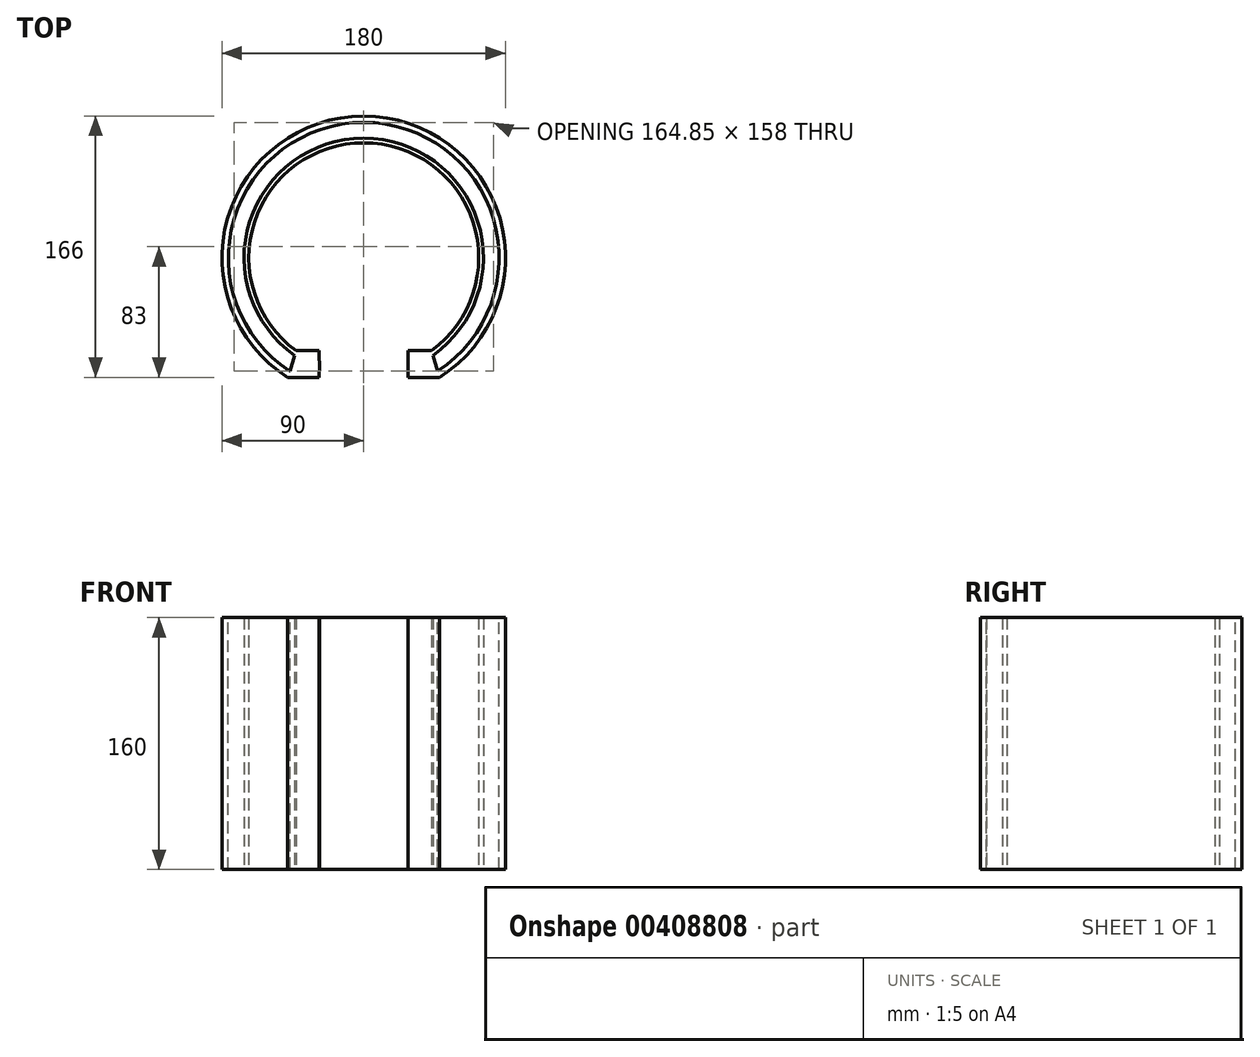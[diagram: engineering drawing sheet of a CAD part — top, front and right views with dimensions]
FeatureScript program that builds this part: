
annotation { "Feature Type Name" : "Feature", "Feature Type Description" : "" }
export const myFeature = defineFeature(function(context is Context, id is Id, definition is map)
    precondition{}
    {
        {
            var Q0;
            Q0=qCreatedBy(makeId("Top.planeOp"),FACE);
            var sketch = newSketch(context, id + "F0", { "sketchPlane" : qUnion([Q0])});
            skArc(sketch, "E0", {"start": v(48.2, -76) * mm, "mid": v(0, 90) * mm, "end": v(-48.2, -76) * mm});
            skLineSegment(sketch, "E1", {"start": v(-48.2, -76) * mm, "end": v(48.2, -76) * mm});
            skCircle(sketch, "E2", {"center": v(0, 0) * mm, "radius": 45 * mm, "construction": true});
            skSolve(sketch);
        }
        {
            var Q0;
            Q0=makeQuery(id+"F0.imprint","IMPRINT",FACE,{"disambiguationData":[TD([[makeQuery(id+"F0.imprint","IMPRINT",EDGE,{"derivedFrom":sQuery(id+"F0.wireOp",EDGE,"E0")}),1.0]])]});
            extrude(context, id + "F1", {"entities" : qUnion([Q0]), "depth" : 160 * mm});
        }
        {
            var Q0;
            Q0=makeQuery(id+"F1.opExtrude","CAP_FACE",FACE,{"disambiguationData":[OSD([sQuery(id+"F0.wireOp",EDGE,"E0"),sQuery(id+"F0.wireOp",EDGE,"E1")])],"isStart":false});
            var sketch = newSketch(context, id + "F2", { "sketchPlane" : qUnion([Q0])});
            skArc(sketch, "E3.0", {"start": v(47.03, -72) * mm, "mid": v(0, 86) * mm, "end": v(-47.03, -72) * mm});
            skLineSegment(sketch, "E3.1", {"start": v(-47.03, -72) * mm, "end": v(47.03, -72) * mm});
            skSolve(sketch);
        }
        {
            var Q0;
            Q0=makeQuery(id+"F2.imprint","IMPRINT",FACE,{"disambiguationData":[TD([[makeQuery(id+"F2.imprint","IMPRINT",EDGE,{"derivedFrom":sQuery(id+"F2.wireOp",EDGE,"E3.0")}),1.0]])]});
            extrude(context, id + "F3", {"entities" : qUnion([Q0]), "operationType" : NewBodyOperationType.REMOVE, "endBound" : BoundingType.UP_TO_NEXT, "oppositeDirection" : true, "depth" : 154 * mm});
        }
        {
            var Q0;
            Q0=makeQuery(id+"F1.opExtrude","SWEPT_FACE",FACE,{"disambiguationData":[OSD([sQuery(id+"F0.wireOp",EDGE,"E1")])]});
            var sketch = newSketch(context, id + "F4", { "sketchPlane" : qUnion([Q0])});
            skLineSegment(sketch, "E4.0", {"start": v(-28.2, 160) * mm, "end": v(-28.2, 0) * mm});
            skLineSegment(sketch, "E5.0", {"start": v(28.2, 160) * mm, "end": v(28.2, 0) * mm});
            skSolve(sketch);
        }
        {
            var Q0;
            Q0=qSketchRegion(id+"F4",true);
            var Q1;
            {var subQ0=sQuery(id+"F4.wireOp",EDGE,"E4.0");Q1=makeQuery(id+"F4.imprint","IMPRINT",FACE,{"disambiguationData":[TD([[makeQuery(id+"F4.imprint","IMPRINT",EDGE,{"derivedFrom":subQ0}),1.0]])]});}
            extrude(context, id + "F5", {"entities" : qUnion([Q0, Q1]), "operationType" : NewBodyOperationType.REMOVE, "endBound" : BoundingType.UP_TO_NEXT, "oppositeDirection" : true, "depth" : 25 * mm});
        }
        {
            var Q0;
            Q0=qCreatedBy(makeId("Top.planeOp"),FACE);
            var sketch = newSketch(context, id + "F6", { "sketchPlane" : qUnion([Q0])});
            skLineSegment(sketch, "E6.0", {"start": v(-43.95, -62) * mm, "end": v(-28.2, -62) * mm});
            skArc(sketch, "E6.1", {"start": v(43.95, -62) * mm, "mid": v(0, 76) * mm, "end": v(-43.95, -62) * mm});
            skLineSegment(sketch, "E6.2", {"start": v(28.2, -62) * mm, "end": v(43.95, -62) * mm});
            skLineSegment(sketch, "E7", {"start": v(-43.95, -62) * mm, "end": v(-46.92, -72.02) * mm});
            skLineSegment(sketch, "E8", {"start": v(-46.92, -72.02) * mm, "end": v(-28.15, -72.02) * mm});
            skLineSegment(sketch, "E9", {"start": v(-28.15, -72.02) * mm, "end": v(-28.2, -59) * mm});
            skLineSegment(sketch, "E10.MirrorCS", {"start": v(43.95, -62) * mm, "end": v(46.92, -72.02) * mm});
            skLineSegment(sketch, "E11.MirrorCS", {"start": v(28.15, -72.02) * mm, "end": v(28.2, -59) * mm});
            skLineSegment(sketch, "E12.MirrorCS", {"start": v(46.92, -72.02) * mm, "end": v(28.15, -72.02) * mm});
            skArc(sketch, "E13.0", {"start": v(42.22, -59.55) * mm, "mid": v(0, 73) * mm, "end": v(-42.22, -59.55) * mm});
            skLineSegment(sketch, "E14.0", {"start": v(-43.95, -59) * mm, "end": v(-28.2, -59) * mm});
            skLineSegment(sketch, "E15.0", {"start": v(28.2, -59) * mm, "end": v(43.95, -59) * mm});
            skSolve(sketch);
        }
        {
            var Q0;
            Q0=qSketchRegion(id+"F6",true);
            extrude(context, id + "F7", {"entities" : qUnion([Q0]), "operationType" : NewBodyOperationType.ADD, "depth" : 160 * mm});
        }
    });
